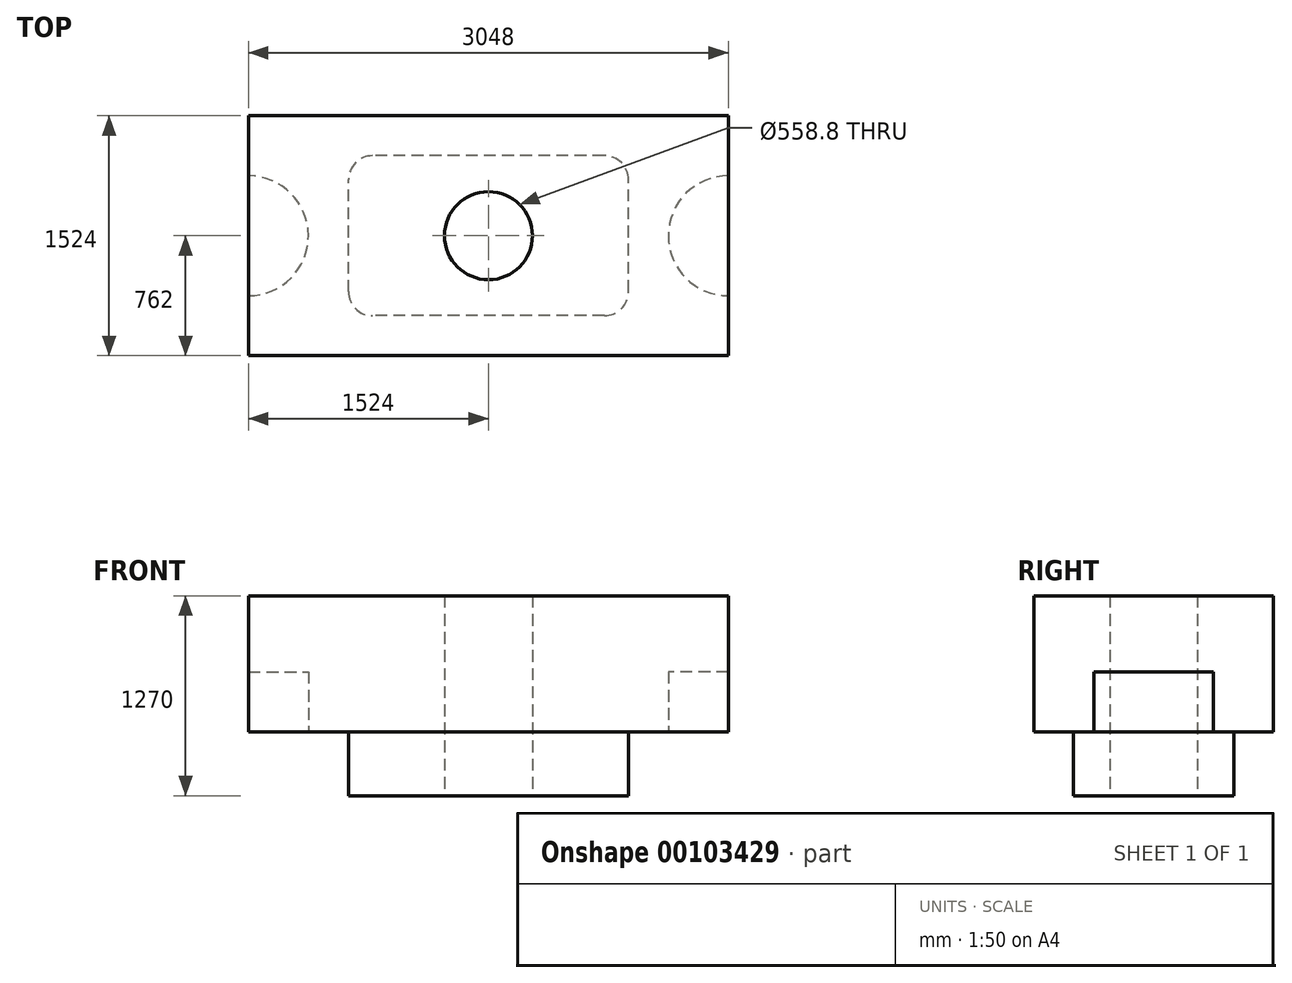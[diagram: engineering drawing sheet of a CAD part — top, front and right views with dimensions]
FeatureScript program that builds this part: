
annotation { "Feature Type Name" : "Feature", "Feature Type Description" : "" }
export const myFeature = defineFeature(function(context is Context, id is Id, definition is map)
    precondition{}
    {
        {
            var Q0;
            Q0=qCreatedBy(makeId("Top.planeOp"),FACE);
            var sketch = newSketch(context, id + "F0", { "sketchPlane" : qUnion([Q0])});
            skLineSegment(sketch, "E0.bottom", {"start": v(1524, -762) * mm, "end": v(-1524, -762) * mm});
            skLineSegment(sketch, "E0.top", {"start": v(1524, 762) * mm, "end": v(-1524, 762) * mm});
            skLineSegment(sketch, "E0.left", {"start": v(1524, -762) * mm, "end": v(1524, 762) * mm});
            skLineSegment(sketch, "E0.right", {"start": v(-1524, -762) * mm, "end": v(-1524, 762) * mm});
            skPoint(sketch, "E0.middle", {"position": v(0, 0) * mm});
            skSolve(sketch);
        }
        {
            var Q0;
            Q0 = qSketchRegion(id + "F0", true);
            extrude(context, id + "F1", {"entities" : qUnion([Q0]), "depth" : 863.6 * mm});
        }
        {
            var Q0;
            Q0=makeQuery(id+"F1.opExtrude","CAP_FACE",FACE,{"disambiguationData":[OSD([sQuery(id+"F0.wireOp",EDGE,"E0.bottom"),sQuery(id+"F0.wireOp",EDGE,"E0.top"),sQuery(id+"F0.wireOp",EDGE,"E0.left"),sQuery(id+"F0.wireOp",EDGE,"E0.right")])],"isStart":true});
            var sketch = newSketch(context, id + "F2", { "sketchPlane" : qUnion([Q0])});
            skArc(sketch, "E1", {"start": v(1524, 381) * mm, "mid": v(1143, 0) * mm, "end": v(1524, -381) * mm});
            skArc(sketch, "E2", {"start": v(-1524, -381) * mm, "mid": v(-1143, 0) * mm, "end": v(-1524, 381) * mm});
            skSolve(sketch);
        }
        {
            var Q0;
            {var subQ0=sQuery(id+"F2.wireOp",EDGE,"E2");Q0=makeQuery(id+"F2.imprint","IMPRINT",FACE,{"disambiguationData":[TD([[makeQuery(id+"F2.imprint","IMPRINT",EDGE,{"derivedFrom":subQ0}),1.0]])]});}
            var Q1;
            {var subQ0=sQuery(id+"F2.wireOp",EDGE,"E1");Q1=makeQuery(id+"F2.imprint","IMPRINT",FACE,{"disambiguationData":[TD([[makeQuery(id+"F2.imprint","IMPRINT",EDGE,{"derivedFrom":subQ0}),1.0]])]});}
            extrude(context, id + "F3", {"entities" : qUnion([Q0, Q1]), "operationType" : NewBodyOperationType.REMOVE, "oppositeDirection" : true, "depth" : 381 * mm});
        }
        {
            var Q0;
            Q0=makeQuery(id+"F1.opExtrude","CAP_FACE",FACE,{"disambiguationData":[OSD([sQuery(id+"F0.wireOp",EDGE,"E0.bottom"),sQuery(id+"F0.wireOp",EDGE,"E0.top"),sQuery(id+"F0.wireOp",EDGE,"E0.left"),sQuery(id+"F0.wireOp",EDGE,"E0.right")])],"isStart":true});
            var sketch = newSketch(context, id + "F4", { "sketchPlane" : qUnion([Q0])});
            skLineSegment(sketch, "E3.bottom", {"start": v(736.6, 508) * mm, "end": v(-736.6, 508) * mm});
            skLineSegment(sketch, "E3.top", {"start": v(736.6, -508) * mm, "end": v(-736.6, -508) * mm});
            skLineSegment(sketch, "E3.left", {"start": v(889, 355.6) * mm, "end": v(889, -355.6) * mm});
            skLineSegment(sketch, "E3.right", {"start": v(-889, 355.6) * mm, "end": v(-889, -355.6) * mm});
            skPoint(sketch, "E3.middle", {"position": v(0, 0) * mm});
            skPoint(sketch, "E4.visualSharp", {"position": v(-889, 508) * mm});
            skArc(sketch, "E4.filletArc", {"start": v(-736.6, 508) * mm, "mid": v(-844.36, 463.36) * mm, "end": v(-889, 355.6) * mm});
            skPoint(sketch, "E5.visualSharp", {"position": v(-889, -508) * mm});
            skArc(sketch, "E5.filletArc", {"start": v(-889, -355.6) * mm, "mid": v(-844.36, -463.36) * mm, "end": v(-736.6, -508) * mm});
            skPoint(sketch, "E6.visualSharp", {"position": v(889, -508) * mm});
            skArc(sketch, "E6.filletArc", {"start": v(736.6, -508) * mm, "mid": v(844.36, -463.36) * mm, "end": v(889, -355.6) * mm});
            skPoint(sketch, "E7.visualSharp", {"position": v(889, 508) * mm});
            skArc(sketch, "E7.filletArc", {"start": v(889, 355.6) * mm, "mid": v(844.36, 463.36) * mm, "end": v(736.6, 508) * mm});
            skSolve(sketch);
        }
        {
            var Q0;
            Q0=makeQuery(id+"F4.imprint","IMPRINT",FACE,{"disambiguationData":[TD([[makeQuery(id+"F4.imprint","IMPRINT",EDGE,{"derivedFrom":sQuery(id+"F4.wireOp",EDGE,"E3.bottom")}),1.0]])]});
            extrude(context, id + "F5", {"entities" : qUnion([Q0]), "operationType" : NewBodyOperationType.ADD, "depth" : 406.4 * mm});
        }
        {
            var Q0;
            Q0=makeQuery(id+"F5.opExtrude","CAP_FACE",FACE,{"disambiguationData":[OSD([sQuery(id+"F4.wireOp",EDGE,"E3.bottom"),sQuery(id+"F4.wireOp",EDGE,"E3.top"),sQuery(id+"F4.wireOp",EDGE,"E3.left"),sQuery(id+"F4.wireOp",EDGE,"E3.right"),sQuery(id+"F4.wireOp",EDGE,"E4.filletArc"),sQuery(id+"F4.wireOp",EDGE,"E5.filletArc"),sQuery(id+"F4.wireOp",EDGE,"E6.filletArc"),sQuery(id+"F4.wireOp",EDGE,"E7.filletArc")])],"isStart":false});
            var sketch = newSketch(context, id + "F6", { "sketchPlane" : qUnion([Q0])});
            skCircle(sketch, "E8", {"center": v(0, 0) * mm, "radius": 279.4 * mm});
            skSolve(sketch);
        }
        {
            var Q0;
            Q0=makeQuery(id+"F6.imprint","IMPRINT",FACE,{"disambiguationData":[TD([[makeQuery(id+"F6.imprint","IMPRINT",EDGE,{"derivedFrom":sQuery(id+"F6.wireOp",EDGE,"E8")}),1.0]])]});
            extrude(context, id + "F7", {"entities" : qUnion([Q0]), "operationType" : NewBodyOperationType.REMOVE, "endBound" : BoundingType.THROUGH_ALL, "oppositeDirection" : true, "depth" : 25.4 * mm});
        }
    });
